# Revit family: C_BTALU520_2DO_Cad_MULT_Prod
name_source: partatom
category: Detail Items
revit_build: Autodesk Revit 2015 (Build: 20140606_1530(x64)
units: mm (PartAtom-declared; Revit-internal decimal feet)

## types (4) — shared parameters
Density = 1.33 kg
Description = Concealed beam hanger
EPD = https://www.strongtie.eu
ETA / DoP = https://www.strongtie.eu
Manufacturer = Simpson Strong-Tie
Model = BTALU520
Model Disclaimer = Contact Simpson Strong-Tie Company  for more information
Model ID = 0064076378931584845029795804671523261148
Name = BTALU520
ObjectType = BTALU520
Product Material = Aluminium
Product Type = Concealed beam hanger
Reference = BTALU520
Technical datasheet = https://www.strongtie.eu
URL = www.strongtie.eu
UniClass Number = Pr_20_29_31_13
UniClass Title = Carbon steel punched metal plate fasteners

## per-type parameters (varying)
| type | _visiblefront | _visibleleft | _visibleright | _visibletop |
| SST_BTALU520_Right | No | No | Yes | No |
| SST_BTALU520_Front | Yes | No | No | No |
| SST_BTALU520_Top | No | No | No | Yes |
| SST_BTALU520_Left | No | Yes | No | No |

## geometry (parser evidence)
native form markers: Sweep x1
no freeform markers — native parametric forms only
